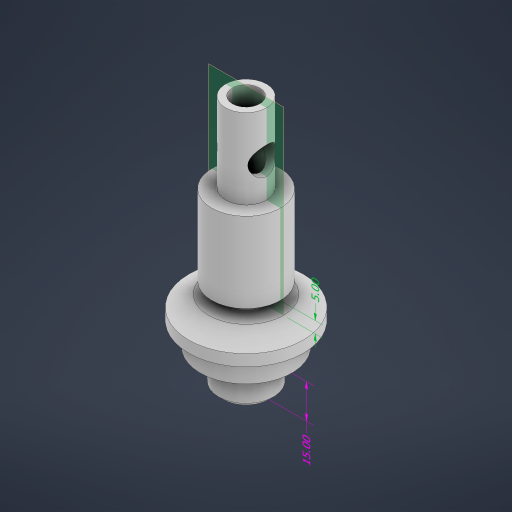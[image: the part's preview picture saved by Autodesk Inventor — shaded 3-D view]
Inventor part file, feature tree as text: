
AUTODESK INVENTOR PART (.ipt)
format: ipt  version: 2024.3 (Build 283343000, 343)  size: 282,112 bytes
history: native  units: mm
features: sketch x10, extrude x8, other x3, plane x1, revolve x1, move_body x1, chamfer x1
ambient origin geometry x8: Origin, YZ Plane, XZ Plane, XY Plane, X Axis, Y Axis, Z Axis, Center Point
bodies: Solid1 (feature_tree)
feature tree (25):
  other  "Annotations"
  extrude  "Extrusion1"  Depth=35.0mm TaperAngle=0.0deg
  extrude  "Extrusion2"  Depth=35.0mm TaperAngle=0.0deg
  extrude  "Extrusion3"  Depth=5.0mm
  plane  "Work Plane1"
  sketch  "Sketch7"  dims[d22=25.0mm d23=90.0deg]
  revolve  "Revolution1"  Angle=90.0deg
  extrude  "Extrusion5"  Depth=40.0mm
  extrude  "Extrusion6"  Depth=10.0mm
  extrude  "Extrusion7"  Depth=12.0mm
  extrude  "Extrusion8"  Depth=12.0mm
  extrude  "Extrusion9"  Depth=15.0mm TaperAngle=0.0deg
  move_body  "Move Body2"
  chamfer  "Chamfer1"  Distance=15.0mm
  sketch  "Sketch2"  dims[d0=18.0mm d1=35.0mm d2=0.0mm]
  sketch  "Sketch3"  dims[d3=30.0mm d4=35.0mm d5=0.0mm]
  sketch  "Sketch4"  dims[d6=5.0mm d7=0.0mm d21=5.0mm]
  sketch  "Sketch8"  dims[d24=5.0mm d25=0.0mm d26=40.0mm]
  sketch  "Sketch9"  dims[d27=10.0mm d28=0.0mm d29=24.0mm]
  sketch  "Sketch10"  dims[d30=15.0mm d31=0.0mm d32=12.0mm]
  sketch  "Sketch11"  dims[d33=120.0mm d34=0.0mm d45=12.0mm]
  sketch  "Sketch12"  dims[d47=15.0mm d48=18.0mm d49=0.0mm]
  sketch  "Sketch13"  dims[d55=90.0deg d56=2.0mm d57=2.0mm d58=45.0deg d38=5.0mm d41=15.0mm]
  other  "Linear Dimension 4"
  other  "Linear Dimension 7"
